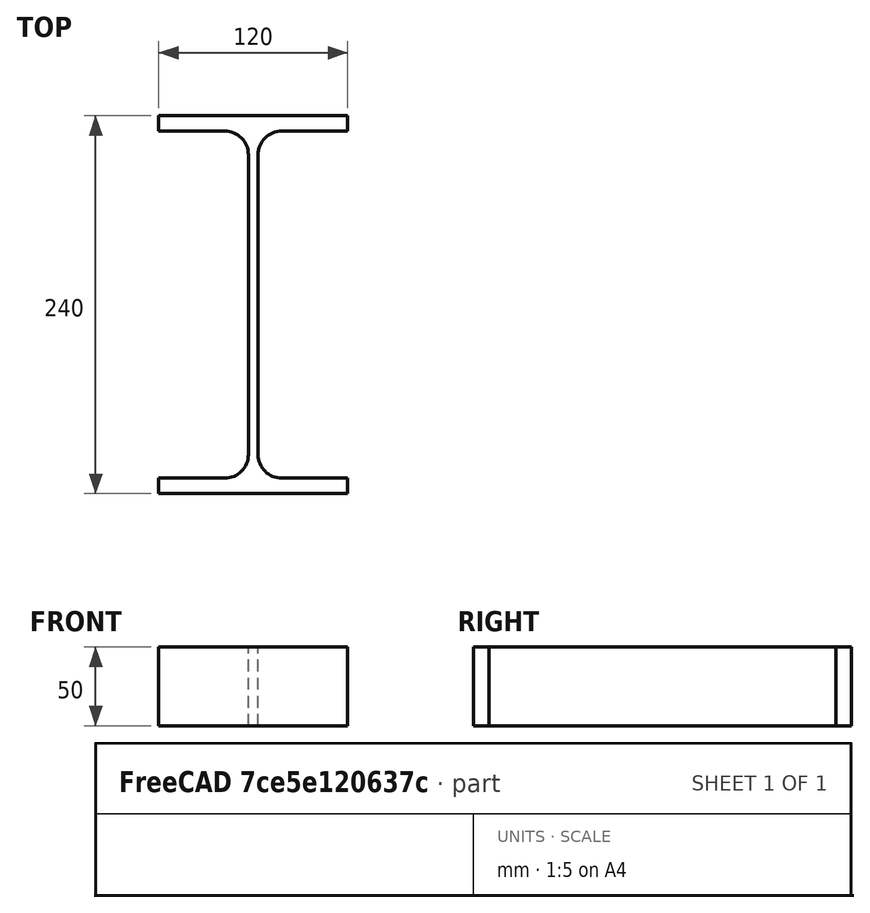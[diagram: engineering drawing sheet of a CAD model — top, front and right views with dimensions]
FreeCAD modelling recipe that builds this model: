
FCSTD DOCUMENT  (FreeCAD 0.15R4671 (Git))
Label: IPE-Profile 240 DIN1025-5 S235JR
License: All rights reserved
LicenseURL: http://en.wikipedia.org/wiki/All_rights_reserved
objects: Sketcher::SketchObject×1, Part::Extrusion×1
note: 2 computed .brp shape members not serialized (recipe doc carries the construction recipe); baked Part::Feature solids carry a one-line shape summary decoded from their .brp

FEATURE [Sketcher::SketchObject] Sketch
  sketch-geometry (16):
    g0: LineSegment StartX=3.1 StartY=-95.2 StartZ=0 EndX=3.1 EndY=95.2 EndZ=0
    g1: LineSegment StartX=18.1 StartY=110.2 StartZ=0 EndX=60 EndY=110.2 EndZ=0
    g2: LineSegment StartX=60 StartY=110.2 StartZ=0 EndX=60 EndY=120 EndZ=0
    g3: LineSegment StartX=60 StartY=120 StartZ=0 EndX=-60 EndY=120 EndZ=0
    g4: LineSegment StartX=-60 StartY=120 StartZ=0 EndX=-60 EndY=110.2 EndZ=0
    g5: LineSegment StartX=-60 StartY=110.2 StartZ=0 EndX=-18.1 EndY=110.2 EndZ=0
    g6: LineSegment StartX=-3.1 StartY=95.2 StartZ=0 EndX=-3.1 EndY=-95.2 EndZ=0
    g7: LineSegment StartX=-18.1 StartY=-110.2 StartZ=0 EndX=-60 EndY=-110.2 EndZ=0
    g8: LineSegment StartX=-60 StartY=-110.2 StartZ=0 EndX=-60 EndY=-120 EndZ=0
    g9: LineSegment StartX=-60 StartY=-120 StartZ=0 EndX=60 EndY=-120 EndZ=0
    g10: LineSegment StartX=60 StartY=-120 StartZ=0 EndX=60 EndY=-110.2 EndZ=0
    g11: LineSegment StartX=60 StartY=-110.2 StartZ=0 EndX=18.1 EndY=-110.2 EndZ=0
    g12: ArcOfCircle CenterX=18.1 CenterY=95.2 CenterZ=0 NormalX=0 NormalY=0 NormalZ=1 Radius=15 StartAngle=1.5708 EndAngle=3.14159
    g13: ArcOfCircle CenterX=18.1 CenterY=-95.2 CenterZ=0 NormalX=0 NormalY=0 NormalZ=1 Radius=15 StartAngle=3.14159 EndAngle=4.71239
    g14: ArcOfCircle CenterX=-18.1 CenterY=95.2 CenterZ=0 NormalX=0 NormalY=0 NormalZ=1 Radius=15 StartAngle=0 EndAngle=1.5708
    g15: ArcOfCircle CenterX=-18.1 CenterY=-95.2 CenterZ=0 NormalX=0 NormalY=0 NormalZ=1 Radius=15 StartAngle=4.71239 EndAngle=6.28319
  constraints (42):
    c: Vertical(g0)
    c: Coincident(g2,g1)
    c: Vertical(g2)
    c: Coincident(g3,g2)
    c: Coincident(g4,g3)
    c: Vertical(g4)
    c: Coincident(g5,g4)
    c: Horizontal(g5)
    c: Vertical(g6)
    c: Horizontal(g7)
    c: Coincident(g8,g7)
    c: Vertical(g8)
    c: Coincident(g9,g8)
    c: Horizontal(g9)
    c: Coincident(g10,g9)
    c: Vertical(g10)
    c: Coincident(g11,g10)
    c: Horizontal(g11)
    c: Tangent(g1,g12) = 1.5708
    c: Tangent(g0,g12) = 1.5708
    c: Tangent(g0,g13) = 1.5708
    c: Tangent(g11,g13) = 1.5708
    c: Tangent(g5,g14) = 1.5708
    c: Tangent(g6,g14) = 1.5708
    c: Tangent(g6,g15) = 1.5708
    c: Tangent(g7,g15) = 1.5708
    c: Equal(g3,g9)
    c: Equal(g2,g4)
    c: Equal(g4,g8)
    c: Equal(g8,g10)
    c: Equal(g12,g14)
    c: Equal(g14,g15)
    c: Equal(g15,g13)
    c: Symmetric(g2,g3,g-2)
    c: Symmetric(g9,g8,g-2)
    c: Symmetric(g0,g6,g-2)
    c: Symmetric(g2,g9,g-1)
    c: DistanceY(g2,g9) = -240
    c: DistanceX(g3) = -120
    c: DistanceX(g0,g6) = -6.2
    c: DistanceY(g2) = 9.8
    c: Radius(g12) = 15
FEATURE [Part::Extrusion] Extrude  label="IPE-Profile 240 DIN1025-5 S235JR"
  Base = -> Sketch
  Dir = (0,0,50)
  Solid = true
